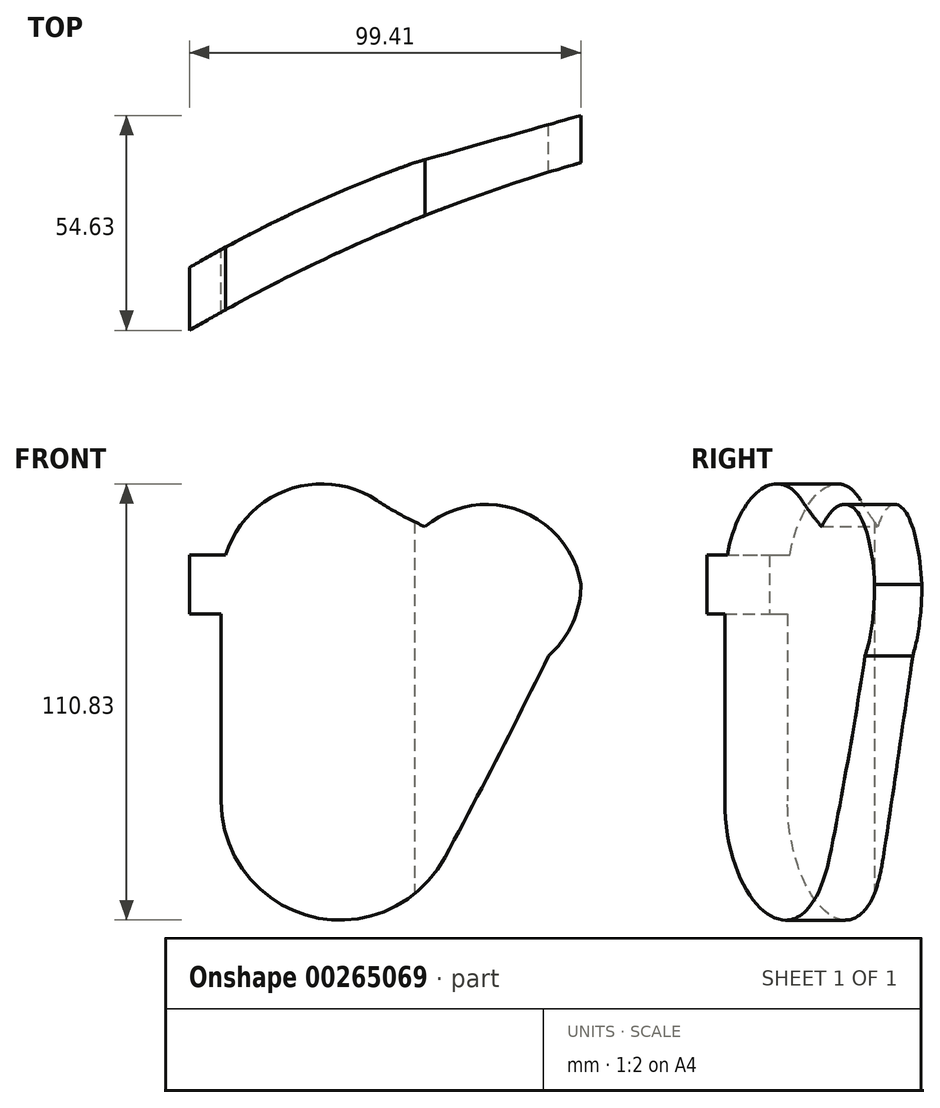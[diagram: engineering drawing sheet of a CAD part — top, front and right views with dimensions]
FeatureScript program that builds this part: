
annotation { "Feature Type Name" : "Feature", "Feature Type Description" : "" }
export const myFeature = defineFeature(function(context is Context, id is Id, definition is map)
    precondition{}
    {
        {
            var Q0;
            Q0=qCreatedBy(makeId("Front.planeOp"),FACE);
            var sketch = newSketch(context, id + "F0", { "sketchPlane" : qUnion([Q0])});
            skArc(sketch, "E0", {"start": v(-25.12, 63.24) * mm, "mid": v(-44.12, 78.7) * mm, "end": v(-63.11, 63.24) * mm});
            skPoint(sketch, "E1", {"position": v(-27.12, 68.67) * mm});
            skArc(sketch, "E2", {"start": v(-58.11, 63.23) * mm, "mid": v(-44.16, 58.33) * mm, "end": v(-30.25, 63.34) * mm});
            skArc(sketch, "E3", {"start": v(-30.25, 63.34) * mm, "mid": v(-44.22, 73.09) * mm, "end": v(-58.11, 63.23) * mm});
            skPoint(sketch, "E4", {"position": v(-44.12, 78.7) * mm});
            skPoint(sketch, "E5", {"position": v(-32.33, 48.34) * mm});
            skArc(sketch, "E6", {"start": v(-63.11, 63.24) * mm, "mid": v(-44.11, 44.24) * mm, "end": v(-25.12, 63.24) * mm});
            skPoint(sketch, "E7", {"position": v(-44.11, 44.24) * mm});
            skPoint(sketch, "E8", {"position": v(-63.11, 63.24) * mm});
            skPoint(sketch, "E9", {"position": v(-58.71, 72.08) * mm});
            skPoint(sketch, "E10", {"position": v(-70.66, 86.37) * mm});
            skArc(sketch, "E11", {"start": v(-59.06, -3.7) * mm, "mid": v(-45.46, 22.2) * mm, "end": v(-32.33, 48.34) * mm});
            skArc(sketch, "E12", {"start": v(-58.71, 72.08) * mm, "mid": v(-66.88, 75.88) * mm, "end": v(-74.64, 80.45) * mm});
            skPoint(sketch, "E13", {"position": v(-31.12, 62.67) * mm});
            skLineSegment(sketch, "E14", {"start": v(-106.53, 63.24) * mm, "end": v(-106.53, 8.24) * mm});
            skArc(sketch, "E15", {"start": v(-74.64, 80.45) * mm, "mid": v(-95.72, 81.35) * mm, "end": v(-106.53, 63.24) * mm});
            skArc(sketch, "E16", {"start": v(-106.53, 8.24) * mm, "mid": v(-87.45, -16.24) * mm, "end": v(-59.06, -3.7) * mm});
            skPoint(sketch, "E17", {"position": v(-86.9, 83.8) * mm});
            skPoint(sketch, "E18", {"position": v(-81.12, -17) * mm});
            skArc(sketch, "E19.0", {"start": v(-54.65, -6.07) * mm, "mid": v(-41.25, 19.43) * mm, "end": v(-28.31, 45.18) * mm});
            skArc(sketch, "E19.1", {"start": v(-59.72, 77.95) * mm, "mid": v(-65.94, 81.05) * mm, "end": v(-71.9, 84.63) * mm});
            skArc(sketch, "E19.2", {"start": v(-71.9, 84.63) * mm, "mid": v(-98.1, 85.75) * mm, "end": v(-111.53, 63.24) * mm});
            skLineSegment(sketch, "E19.3", {"start": v(-111.53, 63.24) * mm, "end": v(-111.53, 8.24) * mm});
            skArc(sketch, "E19.4", {"start": v(-111.53, 8.24) * mm, "mid": v(-88.67, -21.09) * mm, "end": v(-54.65, -6.07) * mm});
            skLineSegment(sketch, "E20", {"start": v(-44.12, 78.7) * mm, "end": v(-44.12, 83.62) * mm});
            skLineSegment(sketch, "E21", {"start": v(-48.78, 91.78) * mm, "end": v(-48.78, 91.78) * mm});
            skLineSegment(sketch, "E22", {"start": v(-25.12, 63.24) * mm, "end": v(-20.12, 63.24) * mm});
            skArc(sketch, "E23", {"start": v(-28.31, 45.18) * mm, "mid": v(-22.26, 53.32) * mm, "end": v(-20.12, 63.24) * mm});
            skArc(sketch, "E24", {"start": v(-44.12, 83.62) * mm, "mid": v(-52.42, 82.16) * mm, "end": v(-59.72, 77.95) * mm});
            skArc(sketch, "E25", {"start": v(-20.12, 63.24) * mm, "mid": v(-28.37, 77.84) * mm, "end": v(-44.12, 83.62) * mm});
            skLineSegment(sketch, "E26", {"start": v(-44.16, 58.29) * mm, "end": v(-44.11, 44.24) * mm});
            skLineSegment(sketch, "E27", {"start": v(-44.12, 78.7) * mm, "end": v(-44.14, 73.09) * mm});
            skPoint(sketch, "E27.endSnap0", {"position": v(-44.14, 51.26) * mm});
            skLineSegment(sketch, "E28", {"start": v(-30.25, 63.34) * mm, "end": v(-25.12, 63.24) * mm});
            skLineSegment(sketch, "E29", {"start": v(-63.11, 63.24) * mm, "end": v(-58.11, 63.23) * mm});
            skLineSegment(sketch, "E30", {"start": v(-40.56, 27.41) * mm, "end": v(-37.18, 27.41) * mm});
            skLineSegment(sketch, "E31", {"start": v(-44.14, 73.09) * mm, "end": v(-44.16, 58.29) * mm});
            skPoint(sketch, "E32", {"position": v(-25.9, 57.86) * mm});
            skArc(sketch, "E33", {"start": v(-27.12, 68.67) * mm, "mid": v(-30.22, 62.84) * mm, "end": v(-25.9, 57.86) * mm});
            skPoint(sketch, "E34", {"position": v(-61.13, 68.62) * mm});
            skPoint(sketch, "E35", {"position": v(-62.33, 57.85) * mm});
            skLineSegment(sketch, "E36.left", {"start": v(-111.53, 63.24) * mm, "end": v(-111.53, 43.24) * mm});
            skLineSegment(sketch, "E36.right", {"start": v(-119.53, 63.24) * mm, "end": v(-119.53, 55.73) * mm});
            skLineSegment(sketch, "E37.left", {"start": v(-111.53, 60.24) * mm, "end": v(-111.53, 46.24) * mm});
            skLineSegment(sketch, "E38.bottom", {"start": v(-25.12, 63.24) * mm, "end": v(-21.5, 63.24) * mm});
            skLineSegment(sketch, "E39.bottom", {"start": v(-25.13, 70.73) * mm, "end": v(-29.13, 70.73) * mm});
            skLineSegment(sketch, "E39.top", {"start": v(-25.13, 55.73) * mm, "end": v(-29.13, 55.73) * mm});
            skLineSegment(sketch, "E39.left", {"start": v(-25.13, 70.73) * mm, "end": v(-25.13, 55.73) * mm});
            skLineSegment(sketch, "E39.right", {"start": v(-29.13, 70.73) * mm, "end": v(-29.13, 55.73) * mm});
            skLineSegment(sketch, "E40", {"start": v(-59.72, 77.95) * mm, "end": v(-58.71, 72.08) * mm});
            skLineSegment(sketch, "E41", {"start": v(-106.53, 63.24) * mm, "end": v(-111.53, 63.24) * mm});
            skLineSegment(sketch, "E42", {"start": v(-63.11, 63.24) * mm, "end": v(-106.53, 63.24) * mm});
            skLineSegment(sketch, "E43", {"start": v(-29.13, 67.73) * mm, "end": v(-25.13, 67.73) * mm});
            skLineSegment(sketch, "E44", {"start": v(-29.13, 58.73) * mm, "end": v(-25.13, 58.73) * mm});
            skPoint(sketch, "E45", {"position": v(-110.4, 70.73) * mm});
            skLineSegment(sketch, "E46", {"start": v(-110.4, 70.73) * mm, "end": v(-59.79, 70.74) * mm});
            skLineSegment(sketch, "E47.bottom", {"start": v(-110.4, 70.73) * mm, "end": v(-119.53, 70.73) * mm});
            skLineSegment(sketch, "E47.top", {"start": v(-111.53, 55.73) * mm, "end": v(-119.53, 55.73) * mm});
            skLineSegment(sketch, "E47.right", {"start": v(-119.53, 70.73) * mm, "end": v(-119.53, 55.73) * mm});
            skLineSegment(sketch, "E48.bottom", {"start": v(-111.13, 67.73) * mm, "end": v(-116.53, 67.73) * mm});
            skLineSegment(sketch, "E48.top", {"start": v(-111.13, 58.73) * mm, "end": v(-116.53, 58.73) * mm});
            skLineSegment(sketch, "E48.right", {"start": v(-116.53, 67.73) * mm, "end": v(-116.53, 58.73) * mm});
            skLineSegment(sketch, "E49.bottom", {"start": v(-111.53, 27.41) * mm, "end": v(-108.53, 27.41) * mm});
            skLineSegment(sketch, "E49.top", {"start": v(-110.88, 2.01) * mm, "end": v(-108.53, 2.01) * mm});
            skLineSegment(sketch, "E49.left", {"start": v(-111.53, 27.41) * mm, "end": v(-111.53, 8.24) * mm});
            skLineSegment(sketch, "E49.right", {"start": v(-108.53, 27.41) * mm, "end": v(-108.53, 2.01) * mm});
            skLineSegment(sketch, "E50.bottom", {"start": v(-50.34, 2.01) * mm, "end": v(-53.07, 2.01) * mm});
            skLineSegment(sketch, "E50.top", {"start": v(-50.34, 2.01) * mm, "end": v(-53.07, 2.01) * mm});
            skLineSegment(sketch, "E50.left", {"start": v(-50.34, 2.01) * mm, "end": v(-50.34, 2.01) * mm});
            skLineSegment(sketch, "E50.right", {"start": v(-53.07, 2.01) * mm, "end": v(-53.07, 2.01) * mm});
            skLineSegment(sketch, "E51", {"start": v(-40.56, 27.41) * mm, "end": v(-53.07, 2.01) * mm});
            skSolve(sketch);
        }
        {
            var Q0;
            Q0=qCreatedBy(makeId("Top.planeOp"),FACE);
            var sketch = newSketch(context, id + "F1", { "sketchPlane" : qUnion([Q0])});
            skLineSegment(sketch, "E52", {"start": v(-20.12, 0) * mm, "end": v(-124.98, 0) * mm});
            skLineSegment(sketch, "E53", {"start": v(-20.12, 0) * mm, "end": v(-62.33, 0) * mm});
            skLineSegment(sketch, "E54", {"start": v(-20.12, 0) * mm, "end": v(-20.12, 29.8) * mm});
            skLineSegment(sketch, "E55", {"start": v(-20.12, 29.8) * mm, "end": v(-124.98, 0) * mm});
            skLineSegment(sketch, "E56", {"start": v(-62.33, 0) * mm, "end": v(-124.98, 0) * mm});
            skLineSegment(sketch, "E57", {"start": v(-20.12, 0) * mm, "end": v(-62.33, -12) * mm});
            skLineSegment(sketch, "E58", {"start": v(-124.98, -29.8) * mm, "end": v(-124.98, 0) * mm});
            skLineSegment(sketch, "E59", {"start": v(-20.12, 0) * mm, "end": v(-20.12, -12) * mm});
            skLineSegment(sketch, "E60", {"start": v(-124.98, -41.93) * mm, "end": v(-124.98, -29.8) * mm});
            skLineSegment(sketch, "E61", {"start": v(-62.33, -12) * mm, "end": v(-62.33, -12) * mm});
            skArc(sketch, "E62", {"start": v(-62.33, -12) * mm, "mid": v(-94.43, -25.34) * mm, "end": v(-124.98, -41.93) * mm});
            skArc(sketch, "E63", {"start": v(-20.12, -12) * mm, "mid": v(-74.1, -31.42) * mm, "end": v(-124.98, -57.9) * mm});
            skLineSegment(sketch, "E64", {"start": v(-124.98, -57.9) * mm, "end": v(-124.98, -41.93) * mm});
            skSolve(sketch);
        }
        {
            var Q0;
            Q0=makeQuery(id+"F1.imprint","IMPRINT",FACE,{"disambiguationData":[TD([[makeQuery(id+"F1.imprint","IMPRINT",EDGE,{"derivedFrom":sQuery(id+"F1.wireOp",EDGE,"E57")}),1.0]])]});
            extrude(context, id + "F2", {"entities" : qUnion([Q0]), "depth" : 250 * mm, "offsetDistance" : 25 * mm, "symmetric" : true});
        }
        {
            var Q0;
            {var subQ0=sQuery(id+"F0.wireOp",EDGE,"E30");Q0=makeQuery(id+"F0.imprint","IMPRINT",FACE,{"disambiguationData":[TD([[makeQuery(id+"F0.imprint","IMPRINT",EDGE,{"derivedFrom":subQ0}),-1.0]])]});}
            var Q1;
            Q1=makeQuery(id+"F0.imprint","IMPRINT",FACE,{"disambiguationData":[TD([[makeQuery(id+"F0.imprint","IMPRINT",EDGE,{"derivedFrom":sQuery(id+"F0.wireOp",EDGE,"E49.bottom")}),-1.0]])]});
            var Q2;
            {var subQ2=sQuery(id+"F0.wireOp",EDGE,"E20");Q2=makeQuery(id+"F0.imprint","IMPRINT",FACE,{"disambiguationData":[TD([[makeQuery(id+"F0.imprint","IMPRINT",EDGE,{"derivedFrom":subQ2}),1.0]])]});}
            var Q3;
            {var subQ5=sQuery(id+"F0.wireOp",EDGE,"E12");Q3=makeQuery(id+"F0.imprint","IMPRINT",FACE,{"disambiguationData":[TD([[makeQuery(id+"F0.imprint","IMPRINT",EDGE,{"derivedFrom":subQ5}),-1.0]])]});}
            var Q4;
            {var subQ1=sQuery(id+"F0.wireOp",EDGE,"E47.bottom");Q4=makeQuery(id+"F0.imprint","IMPRINT",FACE,{"disambiguationData":[TD([[makeQuery(id+"F0.imprint","IMPRINT",EDGE,{"derivedFrom":subQ1}),1.0]])]});}
            var Q5;
            {var subQ0=sQuery(id+"F0.wireOp",EDGE,"E41");Q5=makeQuery(id+"F0.imprint","IMPRINT",FACE,{"disambiguationData":[TD([[makeQuery(id+"F0.imprint","IMPRINT",EDGE,{"derivedFrom":subQ0}),-1.0]])]});}
            var Q6;
            {var subQ0=sQuery(id+"F0.wireOp",EDGE,"E20");Q6=makeQuery(id+"F0.imprint","IMPRINT",FACE,{"disambiguationData":[TD([[makeQuery(id+"F0.imprint","IMPRINT",EDGE,{"derivedFrom":subQ0}),-1.0]])]});}
            var Q7;
            {var subQ17=sQuery(id+"F0.wireOp",EDGE,"E11");Q7=makeQuery(id+"F0.imprint","IMPRINT",FACE,{"disambiguationData":[TD([[makeQuery(id+"F0.imprint","IMPRINT",EDGE,{"derivedFrom":subQ17}),-1.0]])]});}
            var Q8;
            {var subQ0=sQuery(id+"F0.wireOp",EDGE,"E12");Q8=makeQuery(id+"F0.imprint","IMPRINT",FACE,{"disambiguationData":[TD([[makeQuery(id+"F0.imprint","IMPRINT",EDGE,{"derivedFrom":subQ0}),1.0]])]});}
            var Q9;
            {var subQ1=sQuery(id+"F0.wireOp",EDGE,"E2");var subQ3=sQuery(id+"F0.wireOp",EDGE,"E31");var subQ4=makeQuery(id+"F0.imprint","INTERSECT",VERTEX,{"derivedFrom":[subQ1,subQ3]});Q9=makeQuery(id+"F0.imprint","IMPRINT",FACE,{"disambiguationData":[TD([[makeQuery(id+"F0.imprint","IMPRINT",EDGE,{"disambiguationData":[TD([[subQ4,1.0]])],"derivedFrom":subQ1}),1.0]])]});}
            var Q10;
            {var subQ1=sQuery(id+"F0.wireOp",EDGE,"E2");var subQ3=sQuery(id+"F0.wireOp",EDGE,"E31");var subQ4=makeQuery(id+"F0.imprint","INTERSECT",VERTEX,{"derivedFrom":[subQ1,subQ3]});Q10=makeQuery(id+"F0.imprint","IMPRINT",FACE,{"disambiguationData":[TD([[makeQuery(id+"F0.imprint","IMPRINT",EDGE,{"disambiguationData":[TD([[subQ4,1.0]])],"derivedFrom":subQ3}),1.0]])]});}
            var Q11;
            {var subQ9=sQuery(id+"F0.wireOp",EDGE,"E27");Q11=makeQuery(id+"F0.imprint","IMPRINT",FACE,{"disambiguationData":[TD([[makeQuery(id+"F0.imprint","IMPRINT",EDGE,{"derivedFrom":subQ9}),1.0]])]});}
            var Q12;
            {var subQ4=sQuery(id+"F0.wireOp",EDGE,"E27");Q12=makeQuery(id+"F0.imprint","IMPRINT",FACE,{"disambiguationData":[TD([[makeQuery(id+"F0.imprint","IMPRINT",EDGE,{"derivedFrom":subQ4}),-1.0]])]});}
            var Q13;
            {var subQ0=sQuery(id+"F0.wireOp",EDGE,"E26");Q13=makeQuery(id+"F0.imprint","IMPRINT",FACE,{"disambiguationData":[TD([[makeQuery(id+"F0.imprint","IMPRINT",EDGE,{"derivedFrom":subQ0}),1.0]])]});}
            var Q14;
            {var subQ0=sQuery(id+"F0.wireOp",EDGE,"E42");Q14=makeQuery(id+"F0.imprint","IMPRINT",FACE,{"disambiguationData":[TD([[makeQuery(id+"F0.imprint","IMPRINT",EDGE,{"derivedFrom":subQ0}),-1.0]])]});}
            var Q15;
            {var subQ2=sQuery(id+"F0.wireOp",EDGE,"E26");Q15=makeQuery(id+"F0.imprint","IMPRINT",FACE,{"disambiguationData":[TD([[makeQuery(id+"F0.imprint","IMPRINT",EDGE,{"derivedFrom":subQ2}),-1.0]])]});}
            var Q16;
            {var subQ0=sQuery(id+"F0.wireOp",EDGE,"E11");Q16=makeQuery(id+"F0.imprint","IMPRINT",FACE,{"disambiguationData":[TD([[makeQuery(id+"F0.imprint","IMPRINT",EDGE,{"derivedFrom":subQ0}),1.0]])]});}
            var Q17;
            {var subQ7=sQuery(id+"F0.wireOp",EDGE,"E48.bottom");Q17=makeQuery(id+"F0.imprint","IMPRINT",FACE,{"disambiguationData":[TD([[makeQuery(id+"F0.imprint","IMPRINT",EDGE,{"derivedFrom":subQ7}),1.0]])]});}
            var Q18;
            {var subQ0=sQuery(id+"F0.wireOp",EDGE,"E39.right");var subQ1=sQuery(id+"F0.wireOp",EDGE,"E33");var subQ2=makeQuery(id+"F0.imprint","INTERSECT",VERTEX,{"disambiguationData":[OD(1.0)],"derivedFrom":[subQ1,subQ0]});Q18=makeQuery(id+"F0.imprint","IMPRINT",FACE,{"disambiguationData":[TD([[makeQuery(id+"F0.imprint","IMPRINT",EDGE,{"disambiguationData":[TD([[subQ2,-1.0]])],"derivedFrom":subQ1}),-1.0]])]});}
            var Q19;
            {var subQ1=sQuery(id+"F0.wireOp",EDGE,"E28");var subQ3=sQuery(id+"F0.wireOp",EDGE,"E39.right");var subQ4=makeQuery(id+"F0.imprint","INTERSECT",VERTEX,{"derivedFrom":[subQ1,subQ3]});Q19=makeQuery(id+"F0.imprint","IMPRINT",FACE,{"disambiguationData":[TD([[makeQuery(id+"F0.imprint","IMPRINT",EDGE,{"disambiguationData":[TD([[subQ4,1.0]])],"derivedFrom":subQ3}),-1.0]])]});}
            var Q20;
            {var subQ0=sQuery(id+"F0.wireOp",EDGE,"E33");var subQ1=sQuery(id+"F0.wireOp",EDGE,"E0");var subQ2=makeQuery(id+"F0.imprint","INTERSECT",VERTEX,{"derivedFrom":[subQ1,subQ0]});Q20=makeQuery(id+"F0.imprint","IMPRINT",FACE,{"disambiguationData":[TD([[makeQuery(id+"F0.imprint","IMPRINT",EDGE,{"disambiguationData":[TD([[subQ2,1.0]])],"derivedFrom":subQ1}),1.0]])]});}
            var Q21;
            {var subQ0=sQuery(id+"F0.wireOp",EDGE,"E33");var subQ1=sQuery(id+"F0.wireOp",EDGE,"E6");var subQ2=makeQuery(id+"F0.imprint","INTERSECT",VERTEX,{"derivedFrom":[subQ1,subQ0]});Q21=makeQuery(id+"F0.imprint","IMPRINT",FACE,{"disambiguationData":[TD([[makeQuery(id+"F0.imprint","IMPRINT",EDGE,{"disambiguationData":[TD([[subQ2,-1.0]])],"derivedFrom":subQ1}),1.0]])]});}
            var Q22;
            {var subQ1=sQuery(id+"F0.wireOp",EDGE,"E28");var subQ3=sQuery(id+"F0.wireOp",EDGE,"E39.right");var subQ4=makeQuery(id+"F0.imprint","INTERSECT",VERTEX,{"derivedFrom":[subQ1,subQ3]});Q22=makeQuery(id+"F0.imprint","IMPRINT",FACE,{"disambiguationData":[TD([[makeQuery(id+"F0.imprint","IMPRINT",EDGE,{"disambiguationData":[TD([[subQ4,-1.0]])],"derivedFrom":subQ3}),-1.0]])]});}
            var Q23;
            {var subQ5=sQuery(id+"F0.wireOp",EDGE,"E0");var subQ7=makeQuery(id+"F0.imprint","INTERSECT",VERTEX,{"derivedFrom":[subQ5,sQuery(id+"F0.wireOp",EDGE,"E33")]});Q23=makeQuery(id+"F0.imprint","IMPRINT",FACE,{"disambiguationData":[TD([[makeQuery(id+"F0.imprint","IMPRINT",EDGE,{"disambiguationData":[TD([[subQ7,1.0]])],"derivedFrom":subQ5}),-1.0]])]});}
            var Q24;
            {var subQ5=sQuery(id+"F0.wireOp",EDGE,"E33");var subQ6=sQuery(id+"F0.wireOp",EDGE,"E0");var subQ7=makeQuery(id+"F0.imprint","INTERSECT",VERTEX,{"derivedFrom":[subQ6,subQ5]});Q24=makeQuery(id+"F0.imprint","IMPRINT",FACE,{"disambiguationData":[TD([[makeQuery(id+"F0.imprint","IMPRINT",EDGE,{"disambiguationData":[TD([[subQ7,-1.0]])],"derivedFrom":subQ6}),1.0]])]});}
            var Q25;
            {var subQ5=sQuery(id+"F0.wireOp",EDGE,"E33");var subQ6=sQuery(id+"F0.wireOp",EDGE,"E6");var subQ7=makeQuery(id+"F0.imprint","INTERSECT",VERTEX,{"derivedFrom":[subQ6,subQ5]});Q25=makeQuery(id+"F0.imprint","IMPRINT",FACE,{"disambiguationData":[TD([[makeQuery(id+"F0.imprint","IMPRINT",EDGE,{"disambiguationData":[TD([[subQ7,1.0]])],"derivedFrom":subQ6}),1.0]])]});}
            var Q26;
            {var subQ0=sQuery(id+"F0.wireOp",EDGE,"E39.left");var subQ1=sQuery(id+"F0.wireOp",EDGE,"E0");var subQ2=makeQuery(id+"F0.imprint","INTERSECT",VERTEX,{"derivedFrom":[subQ1,subQ0]});Q26=makeQuery(id+"F0.imprint","IMPRINT",FACE,{"disambiguationData":[TD([[makeQuery(id+"F0.imprint","IMPRINT",EDGE,{"disambiguationData":[TD([[subQ2,-1.0]])],"derivedFrom":subQ1}),-1.0]])]});}
            var Q27;
            {var subQ1=sQuery(id+"F0.wireOp",EDGE,"E6");var subQ8=sQuery(id+"F0.wireOp",EDGE,"E44");var subQ11=makeQuery(id+"F0.imprint","INTERSECT",VERTEX,{"derivedFrom":[subQ1,subQ8]});Q27=makeQuery(id+"F0.imprint","IMPRINT",FACE,{"disambiguationData":[TD([[makeQuery(id+"F0.imprint","IMPRINT",EDGE,{"disambiguationData":[TD([[subQ11,-1.0]])],"derivedFrom":subQ1}),1.0]])]});}
            var Q28;
            {var subQ0=sQuery(id+"F0.wireOp",EDGE,"E43");var subQ1=sQuery(id+"F0.wireOp",EDGE,"E33");var subQ2=makeQuery(id+"F0.imprint","INTERSECT",VERTEX,{"derivedFrom":[subQ1,subQ0]});Q28=makeQuery(id+"F0.imprint","IMPRINT",FACE,{"disambiguationData":[TD([[makeQuery(id+"F0.imprint","IMPRINT",EDGE,{"disambiguationData":[TD([[subQ2,-1.0]])],"derivedFrom":subQ1}),-1.0]])]});}
            var Q29;
            {var subQ3=sQuery(id+"F0.wireOp",EDGE,"E6");var subQ8=makeQuery(id+"F0.imprint","INTERSECT",VERTEX,{"derivedFrom":[subQ3,sQuery(id+"F0.wireOp",EDGE,"E33")]});Q29=makeQuery(id+"F0.imprint","IMPRINT",FACE,{"disambiguationData":[TD([[makeQuery(id+"F0.imprint","IMPRINT",EDGE,{"disambiguationData":[TD([[subQ8,1.0]])],"derivedFrom":subQ3}),-1.0]])]});}
            var Q30;
            {var subQ0=sQuery(id+"F0.wireOp",EDGE,"E39.left");var subQ1=sQuery(id+"F0.wireOp",EDGE,"E0");var subQ2=makeQuery(id+"F0.imprint","INTERSECT",VERTEX,{"derivedFrom":[subQ1,subQ0]});Q30=makeQuery(id+"F0.imprint","IMPRINT",FACE,{"disambiguationData":[TD([[makeQuery(id+"F0.imprint","IMPRINT",EDGE,{"disambiguationData":[TD([[subQ2,-1.0]])],"derivedFrom":subQ1}),1.0]])]});}
            var Q31;
            {var subQ0=sQuery(id+"F0.wireOp",EDGE,"E44");var subQ1=sQuery(id+"F0.wireOp",EDGE,"E6");var subQ2=makeQuery(id+"F0.imprint","INTERSECT",VERTEX,{"derivedFrom":[subQ1,subQ0]});Q31=makeQuery(id+"F0.imprint","IMPRINT",FACE,{"disambiguationData":[TD([[makeQuery(id+"F0.imprint","IMPRINT",EDGE,{"disambiguationData":[TD([[subQ2,-1.0]])],"derivedFrom":subQ1}),-1.0]])]});}
            var Q32;
            {var subQ1=sQuery(id+"F0.wireOp",EDGE,"E0");var subQ3=sQuery(id+"F0.wireOp",EDGE,"E39.left");var subQ4=makeQuery(id+"F0.imprint","INTERSECT",VERTEX,{"derivedFrom":[subQ1,subQ3]});Q32=makeQuery(id+"F0.imprint","IMPRINT",FACE,{"disambiguationData":[TD([[makeQuery(id+"F0.imprint","IMPRINT",EDGE,{"disambiguationData":[TD([[subQ4,-1.0]])],"derivedFrom":subQ3}),1.0]])]});}
            var Q33;
            {var subQ1=sQuery(id+"F0.wireOp",EDGE,"E6");var subQ3=sQuery(id+"F0.wireOp",EDGE,"E39.left");var subQ4=makeQuery(id+"F0.imprint","INTERSECT",VERTEX,{"derivedFrom":[subQ1,subQ3]});Q33=makeQuery(id+"F0.imprint","IMPRINT",FACE,{"disambiguationData":[TD([[makeQuery(id+"F0.imprint","IMPRINT",EDGE,{"disambiguationData":[TD([[subQ4,1.0]])],"derivedFrom":subQ3}),1.0]])]});}
            extrude(context, id + "F3", {"entities" : qUnion([Q0, Q1, Q2, Q3, Q4, Q5, Q6, Q7, Q8, Q9, Q10, Q11, Q12, Q13, Q14, Q15, Q16, Q17, Q18, Q19, Q20, Q21, Q22, Q23, Q24, Q25, Q26, Q27, Q28, Q29, Q30, Q31, Q32, Q33]), "operationType" : NewBodyOperationType.INTERSECT, "depth" : 70 * mm, "offsetDistance" : 25 * mm});
        }
    });
